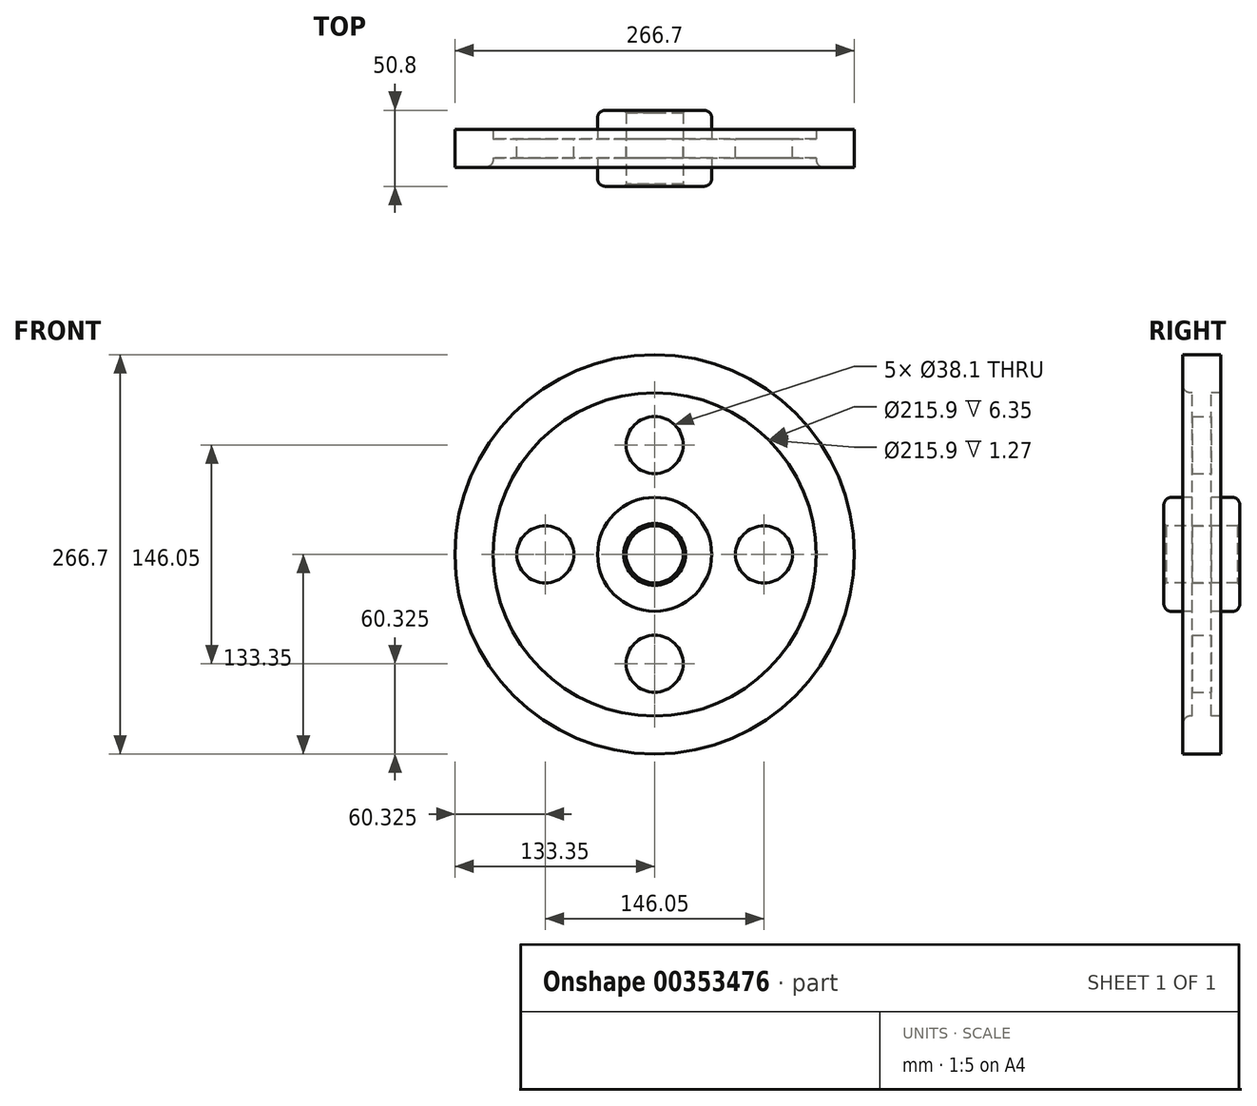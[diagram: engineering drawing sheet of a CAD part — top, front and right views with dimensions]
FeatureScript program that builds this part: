
annotation { "Feature Type Name" : "Feature", "Feature Type Description" : "" }
export const myFeature = defineFeature(function(context is Context, id is Id, definition is map)
    precondition{}
    {
        {
            var Q0;
            Q0=qCreatedBy(makeId("Right.planeOp"),FACE);
            var sketch = newSketch(context, id + "F0", { "sketchPlane" : qUnion([Q0])});
            skLineSegment(sketch, "E0", {"start": v(0, 0) * mm, "end": v(108.18, 0) * mm, "construction": true});
            skLineSegment(sketch, "E1.0", {"start": v(0, 19.05) * mm, "end": v(25.4, 19.05) * mm});
            skLineSegment(sketch, "E2.0", {"start": v(6.35, 38.1) * mm, "end": v(25.4, 38.1) * mm});
            skLineSegment(sketch, "E3.0", {"start": v(6.35, 107.95) * mm, "end": v(12.7, 107.95) * mm});
            skLineSegment(sketch, "E4.0", {"start": v(0, 133.35) * mm, "end": v(12.7, 133.35) * mm});
            skLineSegment(sketch, "E5", {"start": v(0, 133.35) * mm, "end": v(0, 0) * mm, "construction": true});
            skLineSegment(sketch, "E6.0", {"start": v(25.4, 38.1) * mm, "end": v(25.4, 19.05) * mm});
            skLineSegment(sketch, "E7.0", {"start": v(12.7, 133.35) * mm, "end": v(12.7, 107.95) * mm});
            skLineSegment(sketch, "E8.0", {"start": v(6.35, 107.95) * mm, "end": v(6.35, 38.1) * mm});
            skLineSegment(sketch, "E9.MirrorCS", {"start": v(-6.35, 38.1) * mm, "end": v(-25.4, 38.1) * mm});
            skLineSegment(sketch, "E10.MirrorCS", {"start": v(0, 19.05) * mm, "end": v(-25.4, 19.05) * mm});
            skLineSegment(sketch, "E11.MirrorCS", {"start": v(-25.4, 38.1) * mm, "end": v(-25.4, 19.05) * mm});
            skLineSegment(sketch, "E12.MirrorCS", {"start": v(-6.35, 107.95) * mm, "end": v(-6.35, 38.1) * mm});
            skLineSegment(sketch, "E13.MirrorCS", {"start": v(-12.7, 133.35) * mm, "end": v(-12.7, 107.95) * mm});
            skLineSegment(sketch, "E14.MirrorCS", {"start": v(-6.35, 107.95) * mm, "end": v(-12.7, 107.95) * mm});
            skLineSegment(sketch, "E15.MirrorCS", {"start": v(0, 133.35) * mm, "end": v(-12.7, 133.35) * mm});
            skSolve(sketch);
        }
        {
            var Q0;
            Q0=makeQuery(id+"F0.imprint","IMPRINT",FACE,{"disambiguationData":[TD([[makeQuery(id+"F0.imprint","IMPRINT",EDGE,{"derivedFrom":sQuery(id+"F0.wireOp",EDGE,"E1.0")}),1.0]])]});
            var Q1;
            Q1=sQuery(id+"F0.wireOp",EDGE,"E0");
            revolve(context, id + "F1", {"entities" : qUnion([Q0]), "axis" : qUnion([Q1]), "revolveType" : RevolveType.FULL});
        }
        {
            var Q0;
            Q0=makeQuery(id+"F1.opRevolve","SWEPT_FACE",FACE,{"disambiguationData":[OSD([sQuery(id+"F0.wireOp",EDGE,"E8.0")])]});
            var sketch = newSketch(context, id + "F2", { "sketchPlane" : qUnion([Q0])});
            skLineSegment(sketch, "E16", {"start": v(0, 0) * mm, "end": v(0, 73.03) * mm});
            skCircle(sketch, "E17", {"center": v(0, 73.03) * mm, "radius": 19.05 * mm});
            skCircle(sketch, "E18.1.0", {"center": v(-73.03, 0) * mm, "radius": 19.05 * mm});
            skCircle(sketch, "E18.2.0", {"center": v(0, -73.03) * mm, "radius": 19.05 * mm});
            skCircle(sketch, "E18.3.0", {"center": v(73.03, 0) * mm, "radius": 19.05 * mm});
            skPoint(sketch, "E18.center", {"position": v(0, 0) * mm});
            skSolve(sketch);
        }
        {
            var Q0;
            Q0=makeQuery(id+"F2.imprint","IMPRINT",FACE,{"disambiguationData":[TD([[makeQuery(id+"F2.imprint","IMPRINT",EDGE,{"derivedFrom":sQuery(id+"F2.wireOp",EDGE,"E18.1.0")}),1.0]])]});
            var Q1;
            Q1=makeQuery(id+"F2.imprint","IMPRINT",FACE,{"disambiguationData":[TD([[makeQuery(id+"F2.imprint","IMPRINT",EDGE,{"derivedFrom":sQuery(id+"F2.wireOp",EDGE,"E18.3.0")}),1.0]])]});
            var Q2;
            Q2=makeQuery(id+"F2.imprint","IMPRINT",FACE,{"disambiguationData":[TD([[makeQuery(id+"F2.imprint","IMPRINT",EDGE,{"derivedFrom":sQuery(id+"F2.wireOp",EDGE,"E17")}),1.0]])]});
            var Q3;
            Q3=makeQuery(id+"F2.imprint","IMPRINT",FACE,{"disambiguationData":[TD([[makeQuery(id+"F2.imprint","IMPRINT",EDGE,{"derivedFrom":sQuery(id+"F2.wireOp",EDGE,"E18.2.0")}),1.0]])]});
            extrude(context, id + "F3", {"entities" : qUnion([Q0, Q1, Q2, Q3]), "operationType" : NewBodyOperationType.REMOVE, "oppositeDirection" : true, "depth" : 25.4 * mm});
        }
        {
            var Q0;
            Q0=makeQuery(id+"F1.opRevolve","SWEPT_EDGE",EDGE,{"disambiguationData":[OSD([sQuery(id+"F0.wireOp",EDGE,"E9.MirrorCS"),sQuery(id+"F0.wireOp",EDGE,"E11.MirrorCS")])]});
            var Q1;
            Q1=makeQuery(id+"F1.opRevolve","SWEPT_EDGE",EDGE,{"disambiguationData":[OSD([sQuery(id+"F0.wireOp",EDGE,"E13.MirrorCS"),sQuery(id+"F0.wireOp",EDGE,"E14.MirrorCS")])]});
            fillet(context, id + "F4", {"entities" : qUnion([Q0, Q1]), "radius" : 5.08 * mm, "tangentPropagation" : true, "allowEdgeOverflow" : false});
        }
        {
            var Q0;
            Q0=makeQuery(id+"F1.opRevolve","SWEPT_EDGE",EDGE,{"disambiguationData":[OSD([sQuery(id+"F0.wireOp",EDGE,"E10.MirrorCS"),sQuery(id+"F0.wireOp",EDGE,"E11.MirrorCS")])]});
            var Q1;
            Q1=makeQuery(id+"F1.opRevolve","SWEPT_FACE",FACE,{"disambiguationData":[OSD([sQuery(id+"F0.wireOp",EDGE,"E1.0"),sQuery(id+"F0.wireOp",EDGE,"E10.MirrorCS")])]});
            chamfer(context, id + "F5", {"entities" : qUnion([Q0, Q1]), "width" : 1.59 * mm, "tangentPropagation" : true});
        }
        {
            var Q0;
            Q0=makeQuery(id+"F1.opRevolve","SWEPT_EDGE",EDGE,{"disambiguationData":[OSD([sQuery(id+"F0.wireOp",EDGE,"E2.0"),sQuery(id+"F0.wireOp",EDGE,"E6.0")])]});
            fillet(context, id + "F6", {"entities" : qUnion([Q0]), "radius" : 5.08 * mm, "tangentPropagation" : true, "allowEdgeOverflow" : false});
        }
    });
